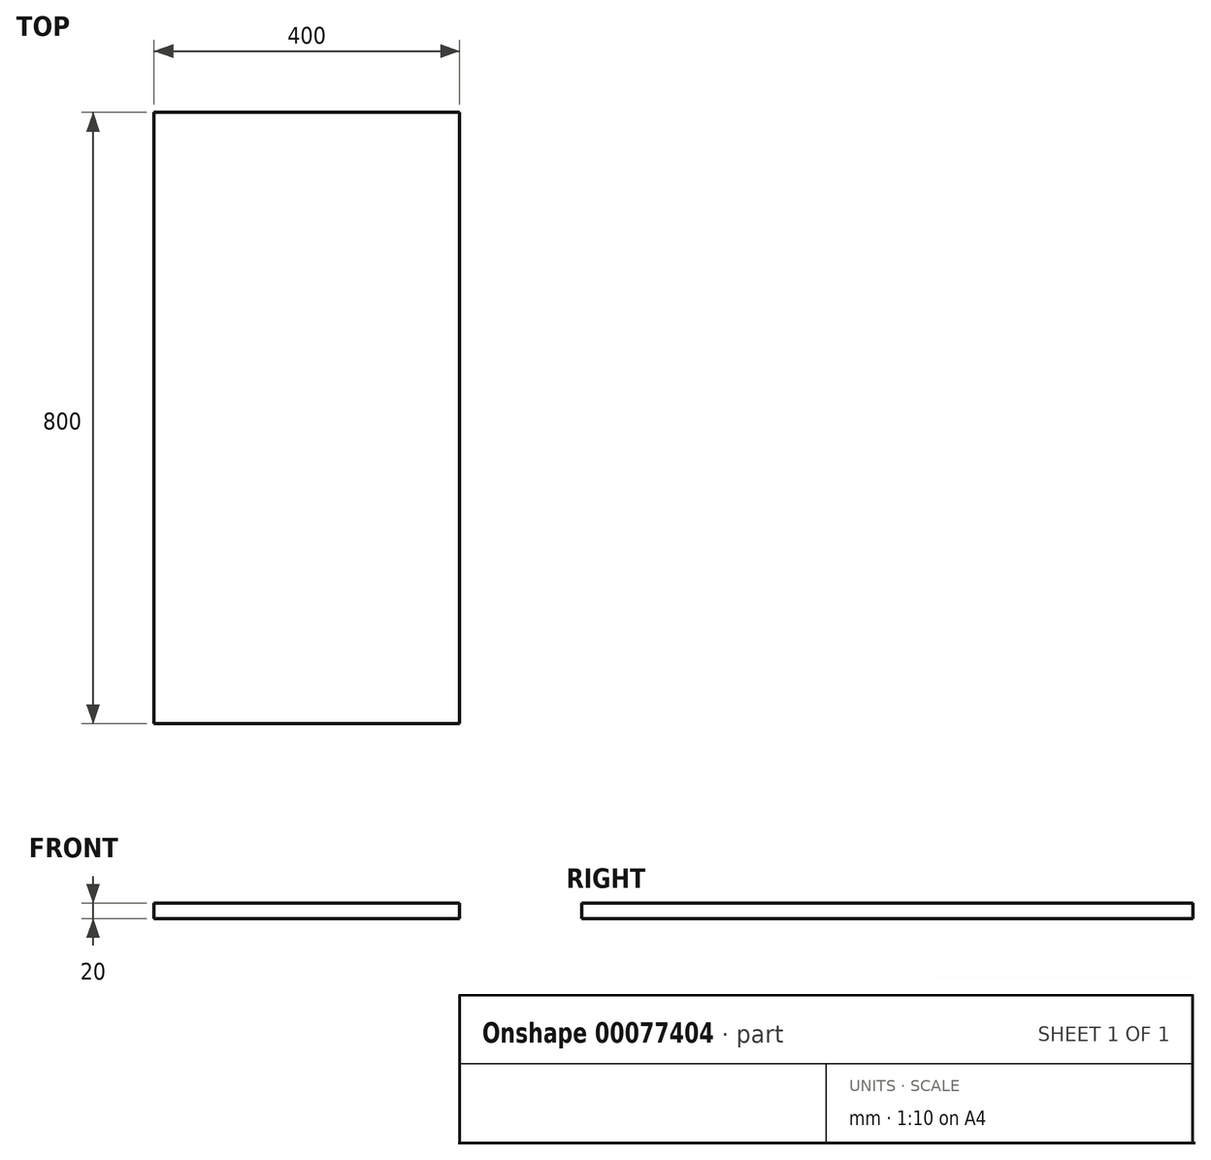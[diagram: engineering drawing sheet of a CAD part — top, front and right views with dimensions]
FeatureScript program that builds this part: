
annotation { "Feature Type Name" : "Feature", "Feature Type Description" : "" }
export const myFeature = defineFeature(function(context is Context, id is Id, definition is map)
    precondition{}
    {
        {
            var Q0;
            Q0=qCreatedBy(makeId("Front.planeOp"),FACE);
            var sketch = newSketch(context, id + "F0", { "sketchPlane" : qUnion([Q0])});
            skLineSegment(sketch, "E0.bottom", {"start": v(-200, 10) * mm, "end": v(200, 10) * mm});
            skLineSegment(sketch, "E0.top", {"start": v(-200, -10) * mm, "end": v(200, -10) * mm});
            skLineSegment(sketch, "E0.left", {"start": v(-200, 10) * mm, "end": v(-200, -10) * mm});
            skLineSegment(sketch, "E0.right", {"start": v(200, 10) * mm, "end": v(200, -10) * mm});
            skPoint(sketch, "E0.middle", {"position": v(0, 0) * mm});
            skSolve(sketch);
        }
        {
            var Q0;
            Q0=makeQuery(id+"F0.imprint","IMPRINT",FACE,{"disambiguationData":[TD([[makeQuery(id+"F0.imprint","IMPRINT",EDGE,{"derivedFrom":sQuery(id+"F0.wireOp",EDGE,"E0.bottom")}),-1.0]])]});
            extrude(context, id + "F1", {"entities" : qUnion([Q0]), "oppositeDirection" : true, "depth" : 800 * mm});
        }
    });
